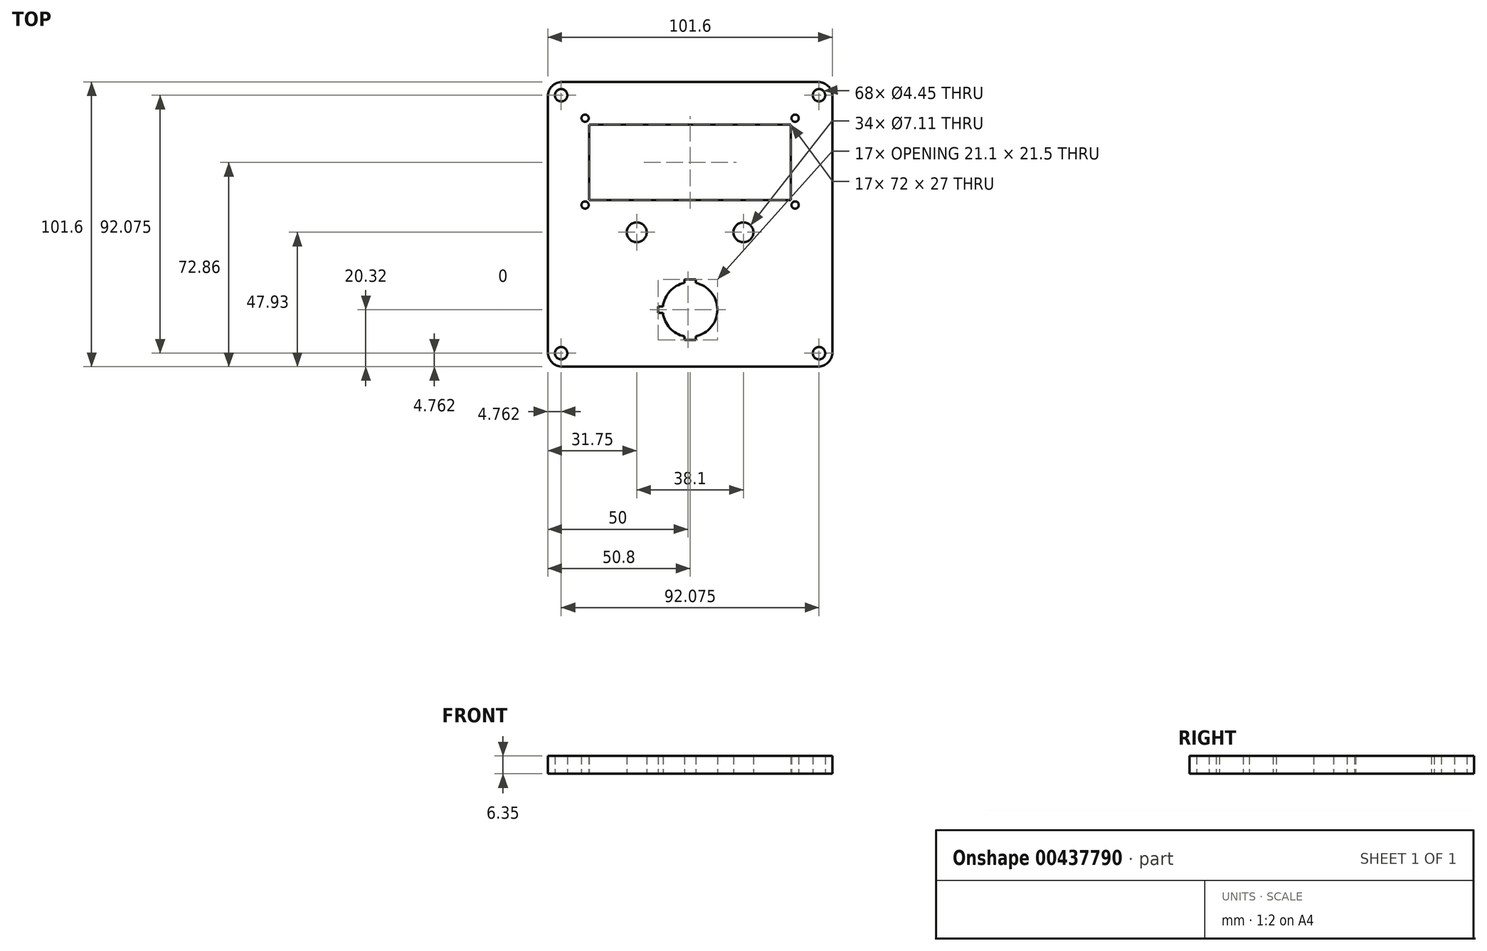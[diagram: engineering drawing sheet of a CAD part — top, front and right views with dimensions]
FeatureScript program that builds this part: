
annotation { "Feature Type Name" : "Feature", "Feature Type Description" : "" }
export const myFeature = defineFeature(function(context is Context, id is Id, definition is map)
    precondition{}
    {
        {
            var Q0;
            Q0=qCreatedBy(makeId("Top.planeOp"),FACE);
            var sketch = newSketch(context, id + "F0", { "sketchPlane" : qUnion([Q0])});
            skLineSegment(sketch, "E0.bottom", {"start": v(-45.72, 50.8) * mm, "end": v(45.72, 50.8) * mm});
            skLineSegment(sketch, "E0.top", {"start": v(-45.72, -50.8) * mm, "end": v(45.72, -50.8) * mm});
            skLineSegment(sketch, "E0.left", {"start": v(-50.8, 45.72) * mm, "end": v(-50.8, -45.72) * mm});
            skLineSegment(sketch, "E0.right", {"start": v(50.8, 45.72) * mm, "end": v(50.8, -45.72) * mm});
            skCircle(sketch, "E1", {"center": v(-46.04, 46.04) * mm, "radius": 2.22 * mm});
            skCircle(sketch, "E2.0.1.0", {"center": v(-46.04, -46.04) * mm, "radius": 2.22 * mm});
            skCircle(sketch, "E2.1.0.0", {"center": v(46.04, 46.04) * mm, "radius": 2.22 * mm});
            skCircle(sketch, "E2.1.1.0", {"center": v(46.04, -46.04) * mm, "radius": 2.22 * mm});
            skLineSegment(sketch, "E2.direction1", {"start": v(-46.04, 46.04) * mm, "end": v(46.04, 46.04) * mm, "construction": true});
            skLineSegment(sketch, "E2.direction2", {"start": v(-46.04, 46.04) * mm, "end": v(-46.04, -46.04) * mm, "construction": true});
            skArc(sketch, "E3", {"start": v(-9.69, -31.58) * mm, "mid": v(-7.2, -37.04) * mm, "end": v(-2, -40.02) * mm});
            skLineSegment(sketch, "E4", {"start": v(0, -30.48) * mm, "end": v(-23.51, -30.48) * mm, "construction": true});
            skLineSegment(sketch, "E5", {"start": v(-11.35, -30.48) * mm, "end": v(-11.35, -29.38) * mm});
            skLineSegment(sketch, "E6", {"start": v(-11.35, -29.38) * mm, "end": v(-9.69, -29.38) * mm});
            skLineSegment(sketch, "E7.MirrorCS", {"start": v(-11.35, -30.48) * mm, "end": v(-11.35, -31.58) * mm});
            skLineSegment(sketch, "E8.MirrorCS", {"start": v(-11.35, -31.58) * mm, "end": v(-9.69, -31.58) * mm});
            skPoint(sketch, "E9", {"position": v(-50.8, 0) * mm});
            skPoint(sketch, "E10", {"position": v(0, 50.8) * mm});
            skPoint(sketch, "E11.visualSharp", {"position": v(-50.8, 50.8) * mm});
            skArc(sketch, "E11.filletArc", {"start": v(-45.72, 50.8) * mm, "mid": v(-49.31, 49.31) * mm, "end": v(-50.8, 45.72) * mm});
            skPoint(sketch, "E12.visualSharp", {"position": v(50.8, 50.8) * mm});
            skArc(sketch, "E12.filletArc", {"start": v(50.8, 45.72) * mm, "mid": v(49.31, 49.31) * mm, "end": v(45.72, 50.8) * mm});
            skPoint(sketch, "E13.visualSharp", {"position": v(50.8, -50.8) * mm});
            skArc(sketch, "E13.filletArc", {"start": v(45.72, -50.8) * mm, "mid": v(49.31, -49.31) * mm, "end": v(50.8, -45.72) * mm});
            skPoint(sketch, "E14.visualSharp", {"position": v(-50.8, -50.8) * mm});
            skArc(sketch, "E14.filletArc", {"start": v(-50.8, -45.72) * mm, "mid": v(-49.31, -49.31) * mm, "end": v(-45.72, -50.8) * mm});
            skCircle(sketch, "E15", {"center": v(-19.05, -2.87) * mm, "radius": 3.56 * mm});
            skCircle(sketch, "E16", {"center": v(-37.5, 37.86) * mm, "radius": 1.3 * mm});
            skCircle(sketch, "E17.0.1.0", {"center": v(-37.5, 6.86) * mm, "radius": 1.3 * mm});
            skCircle(sketch, "E17.1.0.0", {"center": v(37.5, 37.86) * mm, "radius": 1.3 * mm});
            skCircle(sketch, "E17.1.1.0", {"center": v(37.5, 6.86) * mm, "radius": 1.3 * mm});
            skLineSegment(sketch, "E17.direction1", {"start": v(-37.5, 37.86) * mm, "end": v(37.5, 37.86) * mm, "construction": true});
            skLineSegment(sketch, "E17.direction2", {"start": v(-37.5, 37.86) * mm, "end": v(-37.5, 6.86) * mm, "construction": true});
            skLineSegment(sketch, "E18.bottom", {"start": v(36, 8.56) * mm, "end": v(-36, 8.56) * mm});
            skLineSegment(sketch, "E18.top", {"start": v(36, 35.56) * mm, "end": v(-36, 35.56) * mm});
            skLineSegment(sketch, "E18.left", {"start": v(36, 8.56) * mm, "end": v(36, 35.56) * mm});
            skLineSegment(sketch, "E18.right", {"start": v(-36, 8.56) * mm, "end": v(-36, 35.56) * mm});
            skPoint(sketch, "E19", {"position": v(0, 35.56) * mm});
            skPoint(sketch, "E20", {"position": v(0, 37.86) * mm});
            skPoint(sketch, "E21", {"position": v(0, 8.56) * mm});
            skLineSegment(sketch, "E22", {"start": v(0, 37.86) * mm, "end": v(0, 8.56) * mm, "construction": true});
            skCircle(sketch, "E23.MirrorC", {"center": v(19.05, -2.87) * mm, "radius": 3.56 * mm});
            skLineSegment(sketch, "E24", {"start": v(0, -43.55) * mm, "end": v(0, -16.04) * mm, "construction": true});
            skLineSegment(sketch, "E25.bottom", {"start": v(-2, -19.73) * mm, "end": v(2, -19.73) * mm});
            skLineSegment(sketch, "E25.top", {"start": v(-2, -41.23) * mm, "end": v(2, -41.23) * mm});
            skLineSegment(sketch, "E25.left", {"start": v(-2, -19.73) * mm, "end": v(-2, -20.94) * mm});
            skLineSegment(sketch, "E25.right", {"start": v(2, -19.73) * mm, "end": v(2, -20.94) * mm});
            skPoint(sketch, "E26", {"position": v(0, -19.73) * mm});
            skPoint(sketch, "E27", {"position": v(0, -41.23) * mm});
            skArc(sketch, "E28.trimOffspring", {"start": v(-2, -20.94) * mm, "mid": v(-7.2, -23.92) * mm, "end": v(-9.69, -29.38) * mm});
            skArc(sketch, "E29.trimOffspring", {"start": v(2, -40.02) * mm, "mid": v(9.75, -30.48) * mm, "end": v(2, -20.94) * mm});
            skLineSegment(sketch, "E30.trimOffspring", {"start": v(-2, -40.02) * mm, "end": v(-2, -41.23) * mm});
            skLineSegment(sketch, "E31.trimOffspring", {"start": v(2, -40.02) * mm, "end": v(2, -41.23) * mm});
            skSolve(sketch);
        }
        {
            var Q0;
            Q0=makeQuery(id+"F0.imprint","IMPRINT",FACE,{"disambiguationData":[TD([[makeQuery(id+"F0.imprint","IMPRINT",EDGE,{"derivedFrom":sQuery(id+"F0.wireOp",EDGE,"E0.bottom")}),-1.0]])]});
            extrude(context, id + "F1", {"entities" : qUnion([Q0]), "depth" : 6.35 * mm});
        }
    });
